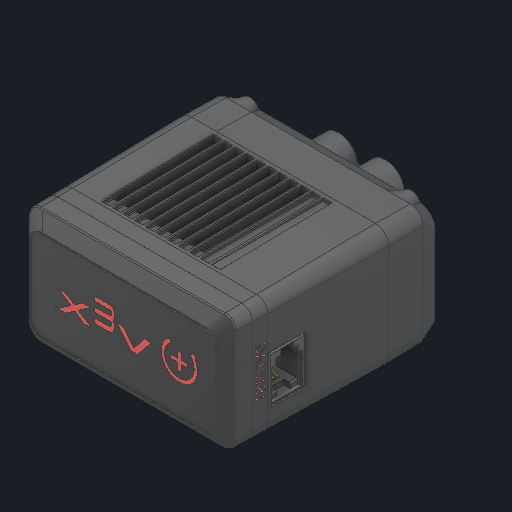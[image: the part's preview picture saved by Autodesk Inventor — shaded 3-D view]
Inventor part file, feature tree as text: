
AUTODESK INVENTOR PART (.ipt)
format: ipt  version: 2024 (Build 280153000, 153)  size: 13,034,496 bytes
history: native  units: in
note: dims shown in document units (in); Inventor stores cm internally (conversion verified against a paired STEP export)
features: other x19, sketch x2
ambient origin geometry x8: Origin, YZ Plane, XZ Plane, XY Plane, X Axis, Y Axis, Z Axis, Center Point
bodies: Solid1 (feature_tree), Solid2 (feature_tree), Solid7 (feature_tree), Solid8 (feature_tree), Solid9 (feature_tree), Solid20 (feature_tree), Solid21 (feature_tree), Solid22 (feature_tree)
feature tree (21):
  other  "V5 Motor.ipt"
  other  "Solid1::V5 Motor.ipt"
  other  "Solid2::V5 Motor.ipt"
  other  "Solid4::V5 Motor.ipt"
  other  "Solid6::V5 Motor.ipt"
  other  "Solid7::V5 Motor.ipt"
  other  "Solid8::V5 Motor.ipt"
  other  "Solid9::V5 Motor.ipt"
  other  "Solid14::V5 Motor.ipt"
  other  "Solid16::V5 Motor.ipt"
  other  "Solid17::V5 Motor.ipt"
  other  "Solid18::V5 Motor.ipt"
  other  "Solid19::V5 Motor.ipt"
  other  "Solid20::V5 Motor.ipt"
  other  "Solid21::V5 Motor.ipt"
  other  "Solid22::V5 Motor.ipt"
  other  "TaggingFeature1"
  sketch  "Sketch1"  dims[d0=0.3937in]
  sketch  "Sketch2"  dims[d4=0.0in d5=0.0in]
  other  "iInsert:1"
  other  "iInsert:2"
